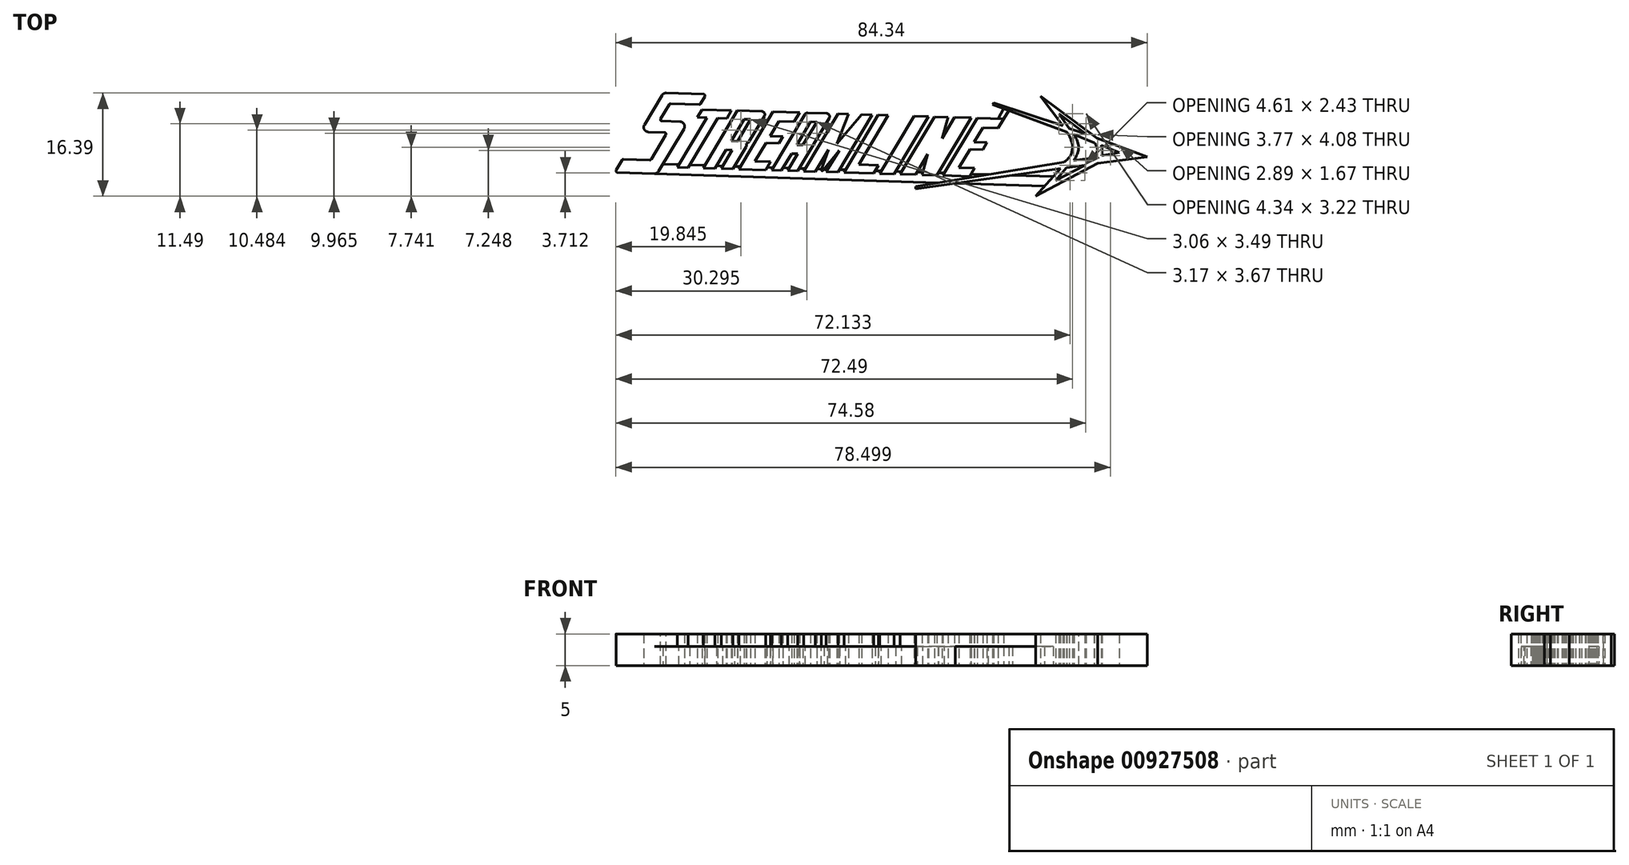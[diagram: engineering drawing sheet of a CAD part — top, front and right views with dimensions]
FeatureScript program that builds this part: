
annotation { "Feature Type Name" : "Feature", "Feature Type Description" : "" }
export const myFeature = defineFeature(function(context is Context, id is Id, definition is map)
    precondition{}
    {
        {
            var Q0;
            Q0=qCreatedBy(makeId("Top.planeOp"),FACE);
            var sketch = newSketch(context, id + "F0", { "sketchPlane" : qUnion([Q0])});
            skLineSegment(sketch, "E0", {"start": v(-39.16, -4.36) * mm, "end": v(-37.92, -2.27) * mm});
            skLineSegment(sketch, "E1", {"start": v(-37.92, -2.27) * mm, "end": v(-33.45, -2.42) * mm});
            skLineSegment(sketch, "E2", {"start": v(-33.45, -2.42) * mm, "end": v(-30.85, 1.96) * mm});
            skLineSegment(sketch, "E3", {"start": v(-30.85, 1.96) * mm, "end": v(-35.11, 2.1) * mm});
            skLineSegment(sketch, "E4", {"start": v(-35.11, 2.1) * mm, "end": v(-31.45, 8.25) * mm});
            skLineSegment(sketch, "E5", {"start": v(-31.45, 8.25) * mm, "end": v(-24.64, 8.03) * mm});
            skLineSegment(sketch, "E6", {"start": v(-24.64, 8.03) * mm, "end": v(-25.6, 6.4) * mm});
            skLineSegment(sketch, "E7", {"start": v(-25.6, 6.4) * mm, "end": v(-30.45, 6.55) * mm});
            skLineSegment(sketch, "E8", {"start": v(-30.45, 6.55) * mm, "end": v(-32.1, 3.8) * mm});
            skLineSegment(sketch, "E9", {"start": v(-32.1, 3.8) * mm, "end": v(-27.53, 3.65) * mm});
            skLineSegment(sketch, "E10", {"start": v(-27.53, 3.65) * mm, "end": v(-32.42, -4.57) * mm});
            skLineSegment(sketch, "E11", {"start": v(-32.42, -4.57) * mm, "end": v(-39.16, -4.36) * mm});
            skLineSegment(sketch, "E12", {"start": v(-29.24, -3.55) * mm, "end": v(-24.55, 4.32) * mm});
            skLineSegment(sketch, "E13", {"start": v(-24.55, 4.32) * mm, "end": v(-26.02, 4.37) * mm});
            skLineSegment(sketch, "E14", {"start": v(-26.02, 4.37) * mm, "end": v(-25.28, 5.61) * mm});
            skLineSegment(sketch, "E15", {"start": v(-25.28, 5.61) * mm, "end": v(-20.64, 5.47) * mm});
            skLineSegment(sketch, "E16", {"start": v(-20.64, 5.47) * mm, "end": v(-21.38, 4.22) * mm});
            skLineSegment(sketch, "E17", {"start": v(-21.38, 4.22) * mm, "end": v(-22.84, 4.27) * mm});
            skLineSegment(sketch, "E18", {"start": v(-22.84, 4.27) * mm, "end": v(-27.53, -3.6) * mm});
            skLineSegment(sketch, "E19", {"start": v(-27.53, -3.6) * mm, "end": v(-29.24, -3.55) * mm});
            skLineSegment(sketch, "E20", {"start": v(-25.11, -3.68) * mm, "end": v(-19.68, 5.44) * mm});
            skLineSegment(sketch, "E21", {"start": v(-19.68, 5.44) * mm, "end": v(-14.98, 5.3) * mm});
            skLineSegment(sketch, "E22", {"start": v(-14.98, 5.3) * mm, "end": v(-17.95, 0.3) * mm});
            skLineSegment(sketch, "E23", {"start": v(-17.95, 0.3) * mm, "end": v(-18.28, 0.22) * mm});
            skLineSegment(sketch, "E24", {"start": v(-18.28, 0.22) * mm, "end": v(-18.2, -0.1) * mm});
            skLineSegment(sketch, "E25", {"start": v(-18.2, -0.1) * mm, "end": v(-20.4, -3.82) * mm});
            skLineSegment(sketch, "E26", {"start": v(-20.4, -3.82) * mm, "end": v(-22.26, -3.77) * mm});
            skLineSegment(sketch, "E27", {"start": v(-22.26, -3.77) * mm, "end": v(-20.5, -0.81) * mm});
            skLineSegment(sketch, "E28", {"start": v(-20.5, -0.81) * mm, "end": v(-21.5, -0.78) * mm});
            skLineSegment(sketch, "E29", {"start": v(-21.5, -0.78) * mm, "end": v(-23.26, -3.74) * mm});
            skLineSegment(sketch, "E30", {"start": v(-23.26, -3.74) * mm, "end": v(-25.11, -3.68) * mm});
            skLineSegment(sketch, "E31", {"start": v(-20.67, 0.62) * mm, "end": v(-18.6, 4.08) * mm});
            skLineSegment(sketch, "E32", {"start": v(-18.6, 4.08) * mm, "end": v(-17.6, 4.05) * mm});
            skLineSegment(sketch, "E33", {"start": v(-17.6, 4.05) * mm, "end": v(-19.67, 0.59) * mm});
            skLineSegment(sketch, "E34", {"start": v(-19.67, 0.59) * mm, "end": v(-20.67, 0.62) * mm});
            skLineSegment(sketch, "E35", {"start": v(-19.45, -3.85) * mm, "end": v(-14.02, 5.26) * mm});
            skLineSegment(sketch, "E36", {"start": v(-14.02, 5.26) * mm, "end": v(-9.8, 5.13) * mm});
            skLineSegment(sketch, "E37", {"start": v(-9.8, 5.13) * mm, "end": v(-10.67, 3.67) * mm});
            skLineSegment(sketch, "E38", {"start": v(-10.67, 3.67) * mm, "end": v(-13.11, 3.74) * mm});
            skLineSegment(sketch, "E39", {"start": v(-13.11, 3.74) * mm, "end": v(-14.5, 1.42) * mm});
            skLineSegment(sketch, "E40", {"start": v(-14.5, 1.42) * mm, "end": v(-12.46, 1.36) * mm});
            skLineSegment(sketch, "E41", {"start": v(-12.46, 1.36) * mm, "end": v(-13.12, 0.24) * mm});
            skLineSegment(sketch, "E42", {"start": v(-13.12, 0.24) * mm, "end": v(-15.16, 0.3) * mm});
            skLineSegment(sketch, "E43", {"start": v(-15.16, 0.3) * mm, "end": v(-16.9, -2.6) * mm});
            skLineSegment(sketch, "E44", {"start": v(-16.9, -2.6) * mm, "end": v(-14.45, -2.68) * mm});
            skLineSegment(sketch, "E45", {"start": v(-14.45, -2.68) * mm, "end": v(-15.23, -3.98) * mm});
            skLineSegment(sketch, "E46", {"start": v(-15.23, -3.98) * mm, "end": v(-19.45, -3.85) * mm});
            skLineSegment(sketch, "E47", {"start": v(-14.28, -4.01) * mm, "end": v(-8.85, 5.1) * mm});
            skLineSegment(sketch, "E48", {"start": v(-8.85, 5.1) * mm, "end": v(-4.68, 4.97) * mm});
            skLineSegment(sketch, "E49", {"start": v(-4.68, 4.97) * mm, "end": v(-10.11, -4.14) * mm});
            skLineSegment(sketch, "E50", {"start": v(-10.11, -4.14) * mm, "end": v(-11.7, -4.1) * mm});
            skLineSegment(sketch, "E51", {"start": v(-11.7, -4.1) * mm, "end": v(-10.09, -1.4) * mm});
            skLineSegment(sketch, "E52", {"start": v(-10.09, -1.4) * mm, "end": v(-11.09, -1.37) * mm});
            skLineSegment(sketch, "E53", {"start": v(-11.09, -1.37) * mm, "end": v(-12.7, -4.06) * mm});
            skLineSegment(sketch, "E54", {"start": v(-12.7, -4.06) * mm, "end": v(-14.28, -4.01) * mm});
            skLineSegment(sketch, "E55", {"start": v(-9.27, -0.02) * mm, "end": v(-7.1, 3.62) * mm});
            skLineSegment(sketch, "E56", {"start": v(-7.1, 3.62) * mm, "end": v(-8.1, 3.65) * mm});
            skLineSegment(sketch, "E57", {"start": v(-8.1, 3.65) * mm, "end": v(-10.27, 0) * mm});
            skLineSegment(sketch, "E58", {"start": v(-10.27, 0) * mm, "end": v(-9.27, -0.02) * mm});
            skLineSegment(sketch, "E59", {"start": v(-9.16, -4.17) * mm, "end": v(-3.73, 4.94) * mm});
            skLineSegment(sketch, "E60", {"start": v(-3.73, 4.94) * mm, "end": v(-2.06, 4.9) * mm});
            skLineSegment(sketch, "E61", {"start": v(-2.06, 4.9) * mm, "end": v(-3.9, 0.18) * mm});
            skLineSegment(sketch, "E62", {"start": v(-3.9, 0.18) * mm, "end": v(0.04, 4.83) * mm});
            skLineSegment(sketch, "E63", {"start": v(0.04, 4.83) * mm, "end": v(1.7, 4.78) * mm});
            skLineSegment(sketch, "E64", {"start": v(1.7, 4.78) * mm, "end": v(-3.72, -4.34) * mm});
            skLineSegment(sketch, "E65", {"start": v(-3.72, -4.34) * mm, "end": v(-5.58, -4.28) * mm});
            skLineSegment(sketch, "E66", {"start": v(-5.58, -4.28) * mm, "end": v(-3.54, -0.86) * mm});
            skLineSegment(sketch, "E67", {"start": v(-3.54, -0.86) * mm, "end": v(-6.67, -4.75) * mm});
            skLineSegment(sketch, "E68", {"start": v(-6.67, -4.75) * mm, "end": v(-5.24, -0.77) * mm});
            skLineSegment(sketch, "E69", {"start": v(-5.24, -0.77) * mm, "end": v(-7.3, -4.23) * mm});
            skLineSegment(sketch, "E70", {"start": v(-7.3, -4.23) * mm, "end": v(-9.16, -4.17) * mm});
            skLineSegment(sketch, "E71", {"start": v(-2.77, -4.37) * mm, "end": v(2.66, 4.75) * mm});
            skLineSegment(sketch, "E72", {"start": v(2.66, 4.75) * mm, "end": v(4.24, 4.7) * mm});
            skLineSegment(sketch, "E73", {"start": v(4.24, 4.7) * mm, "end": v(-0.4, -3.11) * mm});
            skLineSegment(sketch, "E74", {"start": v(-0.4, -3.11) * mm, "end": v(2.74, -3.21) * mm});
            skLineSegment(sketch, "E75", {"start": v(2.74, -3.21) * mm, "end": v(1.96, -4.52) * mm});
            skLineSegment(sketch, "E76", {"start": v(1.96, -4.52) * mm, "end": v(-2.77, -4.37) * mm});
            skLineSegment(sketch, "E77", {"start": v(2.91, -4.55) * mm, "end": v(8.34, 4.57) * mm});
            skLineSegment(sketch, "E78", {"start": v(8.34, 4.57) * mm, "end": v(10.63, 4.5) * mm});
            skLineSegment(sketch, "E79", {"start": v(10.63, 4.5) * mm, "end": v(5.2, -4.62) * mm});
            skLineSegment(sketch, "E80", {"start": v(5.2, -4.62) * mm, "end": v(2.91, -4.55) * mm});
            skLineSegment(sketch, "E81", {"start": v(6.16, -4.65) * mm, "end": v(11.59, 4.47) * mm});
            skLineSegment(sketch, "E82", {"start": v(11.59, 4.47) * mm, "end": v(13.76, 4.4) * mm});
            skLineSegment(sketch, "E83", {"start": v(13.76, 4.4) * mm, "end": v(12.8, 1.04) * mm});
            skLineSegment(sketch, "E84", {"start": v(12.8, 1.04) * mm, "end": v(14.79, 4.37) * mm});
            skLineSegment(sketch, "E85", {"start": v(14.79, 4.37) * mm, "end": v(17.42, 4.29) * mm});
            skLineSegment(sketch, "E86", {"start": v(17.42, 4.29) * mm, "end": v(11.99, -4.83) * mm});
            skLineSegment(sketch, "E87", {"start": v(11.99, -4.83) * mm, "end": v(9.62, -4.75) * mm});
            skLineSegment(sketch, "E88", {"start": v(9.62, -4.75) * mm, "end": v(10.55, -1.49) * mm});
            skLineSegment(sketch, "E89", {"start": v(10.55, -1.49) * mm, "end": v(8.62, -4.72) * mm});
            skLineSegment(sketch, "E90", {"start": v(8.62, -4.72) * mm, "end": v(6.16, -4.65) * mm});
            skLineSegment(sketch, "E91", {"start": v(12.94, -4.86) * mm, "end": v(18.37, 4.26) * mm});
            skLineSegment(sketch, "E92", {"start": v(18.37, 4.26) * mm, "end": v(22.6, 4.13) * mm});
            skLineSegment(sketch, "E93", {"start": v(22.6, 4.13) * mm, "end": v(21.72, 2.66) * mm});
            skLineSegment(sketch, "E94", {"start": v(21.72, 2.66) * mm, "end": v(19.28, 2.74) * mm});
            skLineSegment(sketch, "E95", {"start": v(19.28, 2.74) * mm, "end": v(17.9, 0.42) * mm});
            skLineSegment(sketch, "E96", {"start": v(17.9, 0.42) * mm, "end": v(19.93, 0.35) * mm});
            skLineSegment(sketch, "E97", {"start": v(19.93, 0.35) * mm, "end": v(19.27, -0.76) * mm});
            skLineSegment(sketch, "E98", {"start": v(19.27, -0.76) * mm, "end": v(17.23, -0.7) * mm});
            skLineSegment(sketch, "E99", {"start": v(17.23, -0.7) * mm, "end": v(15.5, -3.6) * mm});
            skLineSegment(sketch, "E100", {"start": v(15.5, -3.6) * mm, "end": v(17.94, -3.68) * mm});
            skLineSegment(sketch, "E101", {"start": v(17.94, -3.68) * mm, "end": v(17.17, -4.99) * mm});
            skLineSegment(sketch, "E102", {"start": v(17.17, -4.99) * mm, "end": v(12.94, -4.86) * mm});
            skLineSegment(sketch, "E103", {"start": v(-17.95, 0.3) * mm, "end": v(-18.2, -0.1) * mm, "construction": true});
            skLineSegment(sketch, "E104", {"start": v(-18.07, 0.1) * mm, "end": v(-18.28, 0.22) * mm, "construction": true});
            skLineSegment(sketch, "E105", {"start": v(-27.53, -3.6) * mm, "end": v(-25.11, -3.68) * mm, "construction": true});
            skLineSegment(sketch, "E106", {"start": v(-23.26, -3.74) * mm, "end": v(-22.26, -3.77) * mm, "construction": true});
            skLineSegment(sketch, "E107", {"start": v(-20.4, -3.82) * mm, "end": v(-19.45, -3.85) * mm, "construction": true});
            skLineSegment(sketch, "E108", {"start": v(-15.23, -3.98) * mm, "end": v(-14.28, -4.01) * mm, "construction": true});
            skLineSegment(sketch, "E109", {"start": v(-12.7, -4.06) * mm, "end": v(-11.7, -4.1) * mm, "construction": true});
            skLineSegment(sketch, "E110", {"start": v(-10.11, -4.14) * mm, "end": v(-9.16, -4.17) * mm, "construction": true});
            skLineSegment(sketch, "E111", {"start": v(-7.3, -4.23) * mm, "end": v(-5.58, -4.28) * mm, "construction": true});
            skLineSegment(sketch, "E112", {"start": v(-3.72, -4.34) * mm, "end": v(-2.77, -4.37) * mm, "construction": true});
            skLineSegment(sketch, "E113", {"start": v(1.96, -4.52) * mm, "end": v(2.91, -4.55) * mm, "construction": true});
            skLineSegment(sketch, "E114", {"start": v(5.2, -4.62) * mm, "end": v(6.16, -4.65) * mm, "construction": true});
            skLineSegment(sketch, "E115", {"start": v(8.62, -4.72) * mm, "end": v(9.62, -4.75) * mm, "construction": true});
            skLineSegment(sketch, "E116", {"start": v(11.99, -4.83) * mm, "end": v(12.94, -4.86) * mm, "construction": true});
            skLineSegment(sketch, "E117", {"start": v(-20.64, 5.47) * mm, "end": v(-19.68, 5.44) * mm, "construction": true});
            skLineSegment(sketch, "E118", {"start": v(-14.98, 5.3) * mm, "end": v(-14.02, 5.26) * mm, "construction": true});
            skLineSegment(sketch, "E119", {"start": v(-9.8, 5.13) * mm, "end": v(-8.85, 5.1) * mm, "construction": true});
            skLineSegment(sketch, "E120", {"start": v(-4.68, 4.97) * mm, "end": v(-3.73, 4.94) * mm, "construction": true});
            skLineSegment(sketch, "E121", {"start": v(-2.06, 4.9) * mm, "end": v(0.04, 4.83) * mm, "construction": true});
            skLineSegment(sketch, "E122", {"start": v(1.7, 4.78) * mm, "end": v(2.66, 4.75) * mm, "construction": true});
            skLineSegment(sketch, "E123", {"start": v(4.24, 4.7) * mm, "end": v(8.34, 4.57) * mm, "construction": true});
            skLineSegment(sketch, "E124", {"start": v(10.63, 4.5) * mm, "end": v(11.59, 4.47) * mm, "construction": true});
            skLineSegment(sketch, "E125", {"start": v(13.76, 4.4) * mm, "end": v(14.79, 4.37) * mm, "construction": true});
            skLineSegment(sketch, "E126", {"start": v(17.42, 4.29) * mm, "end": v(18.37, 4.26) * mm, "construction": true});
            skLineSegment(sketch, "E127", {"start": v(-21.5, -0.78) * mm, "end": v(-20.67, 0.62) * mm, "construction": true});
            skLineSegment(sketch, "E128", {"start": v(-19.67, 0.59) * mm, "end": v(-20.5, -0.81) * mm, "construction": true});
            skLineSegment(sketch, "E129", {"start": v(-10.27, 0) * mm, "end": v(-11.09, -1.37) * mm, "construction": true});
            skLineSegment(sketch, "E130", {"start": v(-9.27, -0.02) * mm, "end": v(-10.09, -1.4) * mm, "construction": true});
            skLineSegment(sketch, "E131", {"start": v(-14.5, 1.42) * mm, "end": v(-15.16, 0.3) * mm, "construction": true});
            skLineSegment(sketch, "E132", {"start": v(17.23, -0.7) * mm, "end": v(17.9, 0.42) * mm, "construction": true});
            skLineSegment(sketch, "E133", {"start": v(-24.55, 4.32) * mm, "end": v(-22.84, 4.27) * mm, "construction": true});
            skSolve(sketch);
        }
        {
            var Q0;
            Q0=qCreatedBy(makeId("Top.planeOp"),FACE);
            var sketch = newSketch(context, id + "F1", { "sketchPlane" : qUnion([Q0])});
            skLineSegment(sketch, "E134", {"start": v(20.83, 6.41) * mm, "end": v(32.6, 2.05) * mm});
            skLineSegment(sketch, "E135", {"start": v(32.16, -2.72) * mm, "end": v(8.64, -6.59) * mm});
            skLineSegment(sketch, "E136", {"start": v(8.64, -6.59) * mm, "end": v(8.64, -6.97) * mm});
            skLineSegment(sketch, "E137", {"start": v(8.64, -6.97) * mm, "end": v(31.59, -3.75) * mm});
            skLineSegment(sketch, "E138", {"start": v(31.59, -3.75) * mm, "end": v(27.65, -8.15) * mm});
            skLineSegment(sketch, "E139", {"start": v(27.65, -8.15) * mm, "end": v(37.48, -2.9) * mm});
            skLineSegment(sketch, "E140", {"start": v(37.48, -2.9) * mm, "end": v(42.24, -2.3) * mm});
            skLineSegment(sketch, "E141", {"start": v(42.2, -0.72) * mm, "end": v(37.4, 1.06) * mm});
            skLineSegment(sketch, "E142", {"start": v(37.4, 1.06) * mm, "end": v(28.42, 7.76) * mm});
            skLineSegment(sketch, "E143", {"start": v(28.42, 7.76) * mm, "end": v(32, 3.03) * mm});
            skLineSegment(sketch, "E144", {"start": v(32, 3.03) * mm, "end": v(20.99, 6.7) * mm});
            skLineSegment(sketch, "E145", {"start": v(20.99, 6.7) * mm, "end": v(20.83, 6.41) * mm});
            skLineSegment(sketch, "E146", {"start": v(31.34, 4.95) * mm, "end": v(35.68, 1.73) * mm});
            skLineSegment(sketch, "E147", {"start": v(35.68, 1.73) * mm, "end": v(33.03, 2.63) * mm});
            skLineSegment(sketch, "E148", {"start": v(33.03, 2.63) * mm, "end": v(31.34, 4.95) * mm});
            skLineSegment(sketch, "E149", {"start": v(30.85, -5.65) * mm, "end": v(35.46, -3.22) * mm});
            skLineSegment(sketch, "E150", {"start": v(35.46, -3.22) * mm, "end": v(32.59, -3.61) * mm});
            skLineSegment(sketch, "E151", {"start": v(32.59, -3.61) * mm, "end": v(30.85, -5.65) * mm});
            skLineSegment(sketch, "E152", {"start": v(38.07, -0.06) * mm, "end": v(40.97, -1.23) * mm});
            skLineSegment(sketch, "E153", {"start": v(40.97, -1.23) * mm, "end": v(38.14, -1.74) * mm});
            skLineSegment(sketch, "E154", {"start": v(33.72, -2.45) * mm, "end": v(36.92, -2.01) * mm});
            skLineSegment(sketch, "E155", {"start": v(37.02, 0.33) * mm, "end": v(33.75, 1.63) * mm});
            skFitSpline(sketch, "E156", {"points": [v(32.6, 2.05) * mm, v(32.66, 1.96) * mm, v(32.9, 1.63) * mm, v(33.25, 0.85) * mm, v(33.52, -0.31) * mm, v(33.25, -1.56) * mm, v(32.67, -2.32) * mm, v(32.28, -2.63) * mm, v(32.16, -2.72) * mm]});
            skFitSpline(sketch, "E157", {"points": [v(38.14, -1.74) * mm, v(38.15, -1.69) * mm, v(38.18, -1.5) * mm, v(38.21, -1.18) * mm, v(38.22, -0.78) * mm, v(38.17, -0.43) * mm, v(38.12, -0.2) * mm, v(38.08, -0.1) * mm, v(38.07, -0.06) * mm]});
            skFitSpline(sketch, "E158", {"points": [v(36.92, -2.01) * mm, v(36.96, -1.94) * mm, v(37.12, -1.7) * mm, v(37.33, -1.3) * mm, v(37.49, -0.74) * mm, v(37.33, -0.24) * mm, v(37.17, 0.1) * mm, v(37.06, 0.28) * mm, v(37.02, 0.33) * mm]});
            skFitSpline(sketch, "E159", {"points": [v(33.75, 1.63) * mm, v(33.82, 1.52) * mm, v(34.02, 1.17) * mm, v(34.32, 0.48) * mm, v(34.5, -0.48) * mm, v(34.27, -1.4) * mm, v(33.98, -2.04) * mm, v(33.78, -2.35) * mm, v(33.72, -2.45) * mm]});
            skLineSegment(sketch, "E160", {"start": v(42.2, -0.72) * mm, "end": v(45.36, -1.9) * mm});
            skLineSegment(sketch, "E161", {"start": v(42.24, -2.3) * mm, "end": v(45.36, -1.9) * mm});
            skSolve(sketch);
        }
        {
            var Q0;
            Q0=qCreatedBy(makeId("Top.planeOp"),FACE);
            var sketch = newSketch(context, id + "F2", { "sketchPlane" : qUnion([Q0])});
            skLineSegment(sketch, "E162", {"start": v(-31.5, -3.03) * mm, "end": v(30.45, -5.02) * mm});
            skLineSegment(sketch, "E163", {"start": v(29.08, -6.55) * mm, "end": v(-32.42, -4.57) * mm});
            skLineSegment(sketch, "E164", {"start": v(30.45, -5.02) * mm, "end": v(29.08, -6.55) * mm});
            skLineSegment(sketch, "E165", {"start": v(22.6, 4.13) * mm, "end": v(23.39, 5.46) * mm});
            skLineSegment(sketch, "E166", {"start": v(22.61, 5.75) * mm, "end": v(21.67, 4.16) * mm});
            skLineSegment(sketch, "E167", {"start": v(21.67, 4.16) * mm, "end": v(22.6, 4.13) * mm});
            skLineSegment(sketch, "E168", {"start": v(22.61, 5.75) * mm, "end": v(23.39, 5.46) * mm});
            skLineSegment(sketch, "E169", {"start": v(-32.42, -4.57) * mm, "end": v(-31.5, -3.03) * mm});
            skSolve(sketch);
        }
        {
            var Q0;
            Q0=makeQuery(id+"F1.imprint","IMPRINT",FACE,{"disambiguationData":[TD([[makeQuery(id+"F1.imprint","IMPRINT",EDGE,{"derivedFrom":sQuery(id+"F1.wireOp",EDGE,"E134")}),1.0]])]});
            extrude(context, id + "F3", {"entities" : qUnion([Q0]), "depth" : 5 * mm, "offsetDistance" : 25 * mm});
        }
        {
            var Q0;
            Q0=makeQuery(id+"F2.imprint","IMPRINT",FACE,{"disambiguationData":[TD([[makeQuery(id+"F2.imprint","IMPRINT",EDGE,{"derivedFrom":sQuery(id+"F2.wireOp",EDGE,"E162")}),-1.0]])]});
            var Q1;
            Q1=makeQuery(id+"F2.imprint","IMPRINT",FACE,{"disambiguationData":[TD([[makeQuery(id+"F2.imprint","IMPRINT",EDGE,{"derivedFrom":sQuery(id+"F2.wireOp",EDGE,"E165")}),1.0]])]});
            extrude(context, id + "F4", {"entities" : qUnion([Q0, Q1]), "operationType" : NewBodyOperationType.ADD, "depth" : 3 * mm, "offsetDistance" : 25 * mm});
        }
        {
            var Q0;
            Q0=qSketchRegion(id+"F0",true);
            extrude(context, id + "F5", {"entities" : qUnion([Q0]), "operationType" : NewBodyOperationType.ADD, "depth" : 5 * mm, "offsetDistance" : 25 * mm});
        }
        {
            var Q0;
            Q0=makeQuery(id+"F5.opExtrude","SWEPT_EDGE",EDGE,{"disambiguationData":[OSD([sQuery(id+"F0.wireOp",EDGE,"E67"),sQuery(id+"F0.wireOp",EDGE,"E68")])]});
            fillet(context, id + "F6", {"entities" : qUnion([Q0]), "radius" : .15 * mm, "tangentPropagation" : true, "allowEdgeOverflow" : false});
        }
        {
            var Q0;
            Q0=makeQuery(id+"F5.opExtrude","SWEPT_EDGE",EDGE,{"disambiguationData":[OSD([sQuery(id+"F0.wireOp",EDGE,"E10"),sQuery(id+"F0.wireOp",EDGE,"E11")])]});
            var Q1;
            Q1=makeQuery(id+"F5.opExtrude","SWEPT_EDGE",EDGE,{"disambiguationData":[OSD([sQuery(id+"F0.wireOp",EDGE,"E9"),sQuery(id+"F0.wireOp",EDGE,"E10")])]});
            var Q2;
            Q2=makeQuery(id+"F5.opExtrude","SWEPT_EDGE",EDGE,{"disambiguationData":[OSD([sQuery(id+"F0.wireOp",EDGE,"E3"),sQuery(id+"F0.wireOp",EDGE,"E4")])]});
            var Q3;
            Q3=makeQuery(id+"F5.opExtrude","SWEPT_EDGE",EDGE,{"disambiguationData":[OSD([sQuery(id+"F0.wireOp",EDGE,"E4"),sQuery(id+"F0.wireOp",EDGE,"E5")])]});
            fillet(context, id + "F7", {"entities" : qUnion([Q0, Q1, Q2, Q3]), "radius" : .75 * mm, "tangentPropagation" : true, "allowEdgeOverflow" : false});
        }
        {
            var Q0;
            Q0=makeQuery(id+"F5.opExtrude","SWEPT_EDGE",EDGE,{"disambiguationData":[OSD([sQuery(id+"F0.wireOp",EDGE,"E6"),sQuery(id+"F0.wireOp",EDGE,"E7")])]});
            var Q1;
            Q1=makeQuery(id+"F5.opExtrude","SWEPT_EDGE",EDGE,{"disambiguationData":[OSD([sQuery(id+"F0.wireOp",EDGE,"E5"),sQuery(id+"F0.wireOp",EDGE,"E6")])]});
            var Q2;
            Q2=makeQuery(id+"F5.opExtrude","SWEPT_EDGE",EDGE,{"disambiguationData":[OSD([sQuery(id+"F0.wireOp",EDGE,"E8"),sQuery(id+"F0.wireOp",EDGE,"E9")])]});
            var Q3;
            Q3=makeQuery(id+"F5.opExtrude","SWEPT_EDGE",EDGE,{"disambiguationData":[OSD([sQuery(id+"F0.wireOp",EDGE,"E2"),sQuery(id+"F0.wireOp",EDGE,"E3")])]});
            var Q4;
            Q4=makeQuery(id+"F5.opExtrude","SWEPT_EDGE",EDGE,{"disambiguationData":[OSD([sQuery(id+"F0.wireOp",EDGE,"E1"),sQuery(id+"F0.wireOp",EDGE,"E2")])]});
            var Q5;
            Q5=makeQuery(id+"F5.opExtrude","SWEPT_EDGE",EDGE,{"disambiguationData":[OSD([sQuery(id+"F0.wireOp",EDGE,"E0"),sQuery(id+"F0.wireOp",EDGE,"E1")])]});
            var Q6;
            Q6=makeQuery(id+"F5.opExtrude","SWEPT_EDGE",EDGE,{"disambiguationData":[OSD([sQuery(id+"F0.wireOp",EDGE,"E0"),sQuery(id+"F0.wireOp",EDGE,"E11")])]});
            var Q7;
            Q7=makeQuery(id+"F5.opExtrude","SWEPT_EDGE",EDGE,{"disambiguationData":[OSD([sQuery(id+"F0.wireOp",EDGE,"E7"),sQuery(id+"F0.wireOp",EDGE,"E8")])]});
            fillet(context, id + "F8", {"entities" : qUnion([Q0, Q1, Q2, Q3, Q4, Q5, Q6, Q7]), "radius" : .25 * mm, "tangentPropagation" : true, "allowEdgeOverflow" : false});
        }
        {
            var Q0;
            Q0=makeQuery(id+"F5.opExtrude","SWEPT_EDGE",EDGE,{"disambiguationData":[OSD([sQuery(id+"F0.wireOp",EDGE,"E21"),sQuery(id+"F0.wireOp",EDGE,"E22")])]});
            var Q1;
            Q1=makeQuery(id+"F5.opExtrude","SWEPT_EDGE",EDGE,{"disambiguationData":[OSD([sQuery(id+"F0.wireOp",EDGE,"E47"),sQuery(id+"F0.wireOp",EDGE,"E48")])]});
            var Q2;
            Q2=makeQuery(id+"F5.opExtrude","SWEPT_EDGE",EDGE,{"disambiguationData":[OSD([sQuery(id+"F0.wireOp",EDGE,"E48"),sQuery(id+"F0.wireOp",EDGE,"E49")])]});
            var Q3;
            Q3=makeQuery(id+"F5.opExtrude","SWEPT_EDGE",EDGE,{"disambiguationData":[OSD([sQuery(id+"F0.wireOp",EDGE,"E22"),sQuery(id+"F0.wireOp",EDGE,"E23")])]});
            var Q4;
            Q4=makeQuery(id+"F5.opExtrude","SWEPT_EDGE",EDGE,{"disambiguationData":[OSD([sQuery(id+"F0.wireOp",EDGE,"E24"),sQuery(id+"F0.wireOp",EDGE,"E25")])]});
            fillet(context, id + "F9", {"entities" : qUnion([Q0, Q1, Q2, Q3, Q4]), "radius" : .5 * mm, "tangentPropagation" : true, "allowEdgeOverflow" : false});
        }
    });
